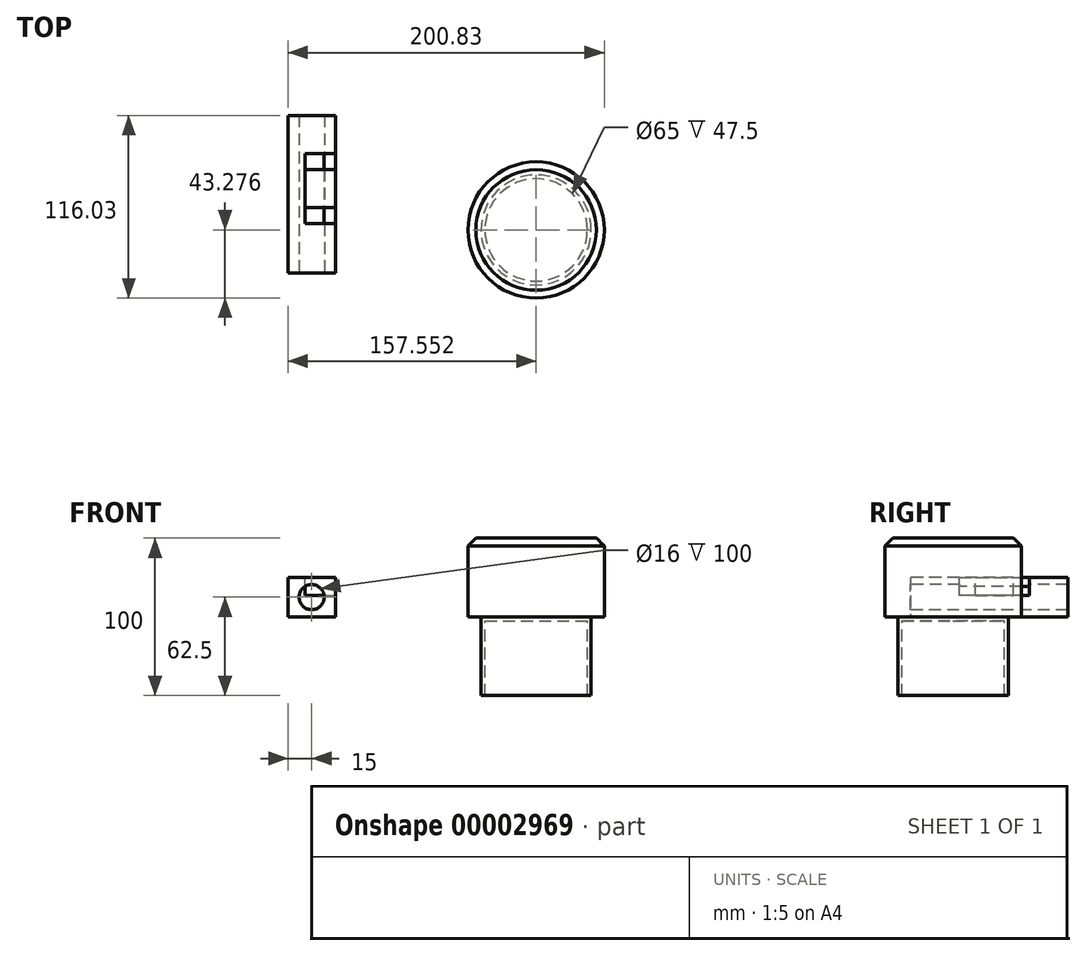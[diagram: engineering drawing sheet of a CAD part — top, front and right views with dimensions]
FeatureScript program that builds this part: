
annotation { "Feature Type Name" : "Feature", "Feature Type Description" : "" }
export const myFeature = defineFeature(function(context is Context, id is Id, definition is map)
    precondition{}
    {
        {
            var Q0;
            Q0=qCreatedBy(makeId("Top.planeOp"),FACE);
            var sketch = newSketch(context, id + "F0", { "sketchPlane" : qUnion([Q0])});
            skLineSegment(sketch, "E0.bottom", {"start": v(0, 0) * mm, "end": v(30, 0) * mm});
            skLineSegment(sketch, "E0.top", {"start": v(0, -100) * mm, "end": v(30, -100) * mm});
            skLineSegment(sketch, "E0.left", {"start": v(0, 0) * mm, "end": v(0, -100) * mm});
            skLineSegment(sketch, "E0.right", {"start": v(30, 0) * mm, "end": v(30, -100) * mm});
            skCircle(sketch, "E1", {"center": v(157.55, -72.75) * mm, "radius": 43.28 * mm});
            skSolve(sketch);
        }
        {
            var Q0;
            Q0=makeQuery(id+"F0.imprint","IMPRINT",FACE,{"disambiguationData":[TD([[makeQuery(id+"F0.imprint","IMPRINT",EDGE,{"derivedFrom":sQuery(id+"F0.wireOp",EDGE,"E0.bottom")}),-1.0]])]});
            var Q1;
            Q1=makeQuery(id+"F0.imprint","IMPRINT",FACE,{"disambiguationData":[TD([[makeQuery(id+"F0.imprint","IMPRINT",EDGE,{"derivedFrom":sQuery(id+"F0.wireOp",EDGE,"E1")}),1.0]])]});
            extrude(context, id + "F1", {"entities" : qUnion([Q0, Q1]), "depth" : 25 * mm});
        }
        {
            var Q0;
            Q0=makeQuery(id+"F1.opExtrude","SWEPT_FACE",FACE,{"disambiguationData":[OSD([sQuery(id+"F0.wireOp",EDGE,"E0.top")])]});
            var sketch = newSketch(context, id + "F2", { "sketchPlane" : qUnion([Q0])});
            skCircle(sketch, "E2", {"center": v(15, 12.5) * mm, "radius": 8 * mm});
            skLineSegment(sketch, "E3", {"start": v(30, 25) * mm, "end": v(0, 0) * mm});
            skSolve(sketch);
        }
        {
            var Q0;
            {var subQ0=sQuery(id+"F2.wireOp",EDGE,"E3");var subQ1=sQuery(id+"F2.wireOp",EDGE,"E2");var subQ3=makeQuery(id+"F2.imprint","INTERSECT",VERTEX,{"disambiguationData":[OD(0.0)],"derivedFrom":[subQ1,subQ0]});Q0=qUnion([makeQuery(id+"F2.imprint","IMPRINT",FACE,{"disambiguationData":[TD([[makeQuery(id+"F2.imprint","IMPRINT",EDGE,{"disambiguationData":[TD([[subQ3,-1.0]])],"derivedFrom":subQ1}),1.0]])]}),makeQuery(id+"F2.imprint","IMPRINT",FACE,{"disambiguationData":[TD([[makeQuery(id+"F2.imprint","IMPRINT",EDGE,{"disambiguationData":[TD([[subQ3,1.0]])],"derivedFrom":subQ1}),1.0]])]})]);}
            extrude(context, id + "F3", {"entities" : qUnion([Q0]), "operationType" : NewBodyOperationType.REMOVE, "endBound" : BoundingType.THROUGH_ALL, "oppositeDirection" : true, "depth" : 25 * mm});
        }
        {
            var Q0;
            Q0=makeQuery(id+"F1.opExtrude","CAP_FACE",FACE,{"disambiguationData":[OSD([sQuery(id+"F0.wireOp",EDGE,"E1")])],"isStart":true});
            var sketch = newSketch(context, id + "F4", { "sketchPlane" : qUnion([Q0])});
            skCircle(sketch, "E4", {"center": v(157.55, 72.75) * mm, "radius": 35 * mm});
            skSolve(sketch);
        }
        {
            var Q0;
            Q0=makeQuery(id+"F4.imprint","IMPRINT",FACE,{"disambiguationData":[TD([[makeQuery(id+"F4.imprint","IMPRINT",EDGE,{"derivedFrom":sQuery(id+"F4.wireOp",EDGE,"E4")}),1.0]])]});
            extrude(context, id + "F5", {"entities" : qUnion([Q0]), "depth" : 50 * mm});
        }
        {
            var Q0;
            Q0=makeQuery(id+"F1.opExtrude","CAP_FACE",FACE,{"disambiguationData":[OSD([sQuery(id+"F0.wireOp",EDGE,"E1")])],"isStart":false});
            extrude(context, id + "F6", {"entities" : qUnion([Q0]), "operationType" : NewBodyOperationType.ADD, "depth" : 25 * mm});
        }
        {
            var Q0;
            Q0=makeQuery(id+"F6.opExtrude","CAP_FACE",FACE,{"disambiguationData":[OSD([sQuery(id+"F0.wireOp",EDGE,"E1")])],"isStart":false});
            chamfer(context, id + "F7", {"entities" : qUnion([Q0]), "width" : 5 * mm, "tangentPropagation" : true});
        }
        {
            var Q0;
            Q0=makeQuery(id+"F5.opExtrude","CAP_FACE",FACE,{"disambiguationData":[OSD([sQuery(id+"F4.wireOp",EDGE,"E4")])],"isStart":false});
            shell(context, id + "F8", {"entities" : qUnion([Q0]), "thickness" : 2.5 * mm});
        }
        {
            var Q0;
            Q0=makeQuery(id+"F1.opExtrude","CAP_FACE",FACE,{"disambiguationData":[OSD([sQuery(id+"F0.wireOp",EDGE,"E0.bottom"),sQuery(id+"F0.wireOp",EDGE,"E0.top"),sQuery(id+"F0.wireOp",EDGE,"E0.left"),sQuery(id+"F0.wireOp",EDGE,"E0.right")])],"isStart":false});
            var sketch = newSketch(context, id + "F9", { "sketchPlane" : qUnion([Q0])});
            skLineSegment(sketch, "E5.bottom", {"start": v(10.71, -58.64) * mm, "end": v(30, -58.64) * mm});
            skLineSegment(sketch, "E5.top", {"start": v(10.71, -34.43) * mm, "end": v(30, -34.43) * mm});
            skLineSegment(sketch, "E5.left", {"start": v(10.71, -58.64) * mm, "end": v(10.71, -34.43) * mm});
            skLineSegment(sketch, "E5.right", {"start": v(30, -58.64) * mm, "end": v(30, -34.43) * mm});
            skSolve(sketch);
        }
        {
            var Q0;
            Q0=makeQuery(id+"F9.imprint","IMPRINT",FACE,{"disambiguationData":[TD([[makeQuery(id+"F9.imprint","IMPRINT",EDGE,{"derivedFrom":sQuery(id+"F9.wireOp",EDGE,"E5.bottom")}),1.0]])]});
            extrude(context, id + "F10", {"entities" : qUnion([Q0]), "oppositeDirection" : true, "depth" : 11.33 * mm});
        }
        {
            var Q0;
            Q0=makeQuery(id+"F10.opExtrude","SWEPT_BODY",BODY,{"disambiguationData":[OSD([sQuery(id+"F9.wireOp",EDGE,"E5.bottom"),sQuery(id+"F9.wireOp",EDGE,"E5.top"),sQuery(id+"F9.wireOp",EDGE,"E5.left"),sQuery(id+"F9.wireOp",EDGE,"E5.right")])]});
            var Q1;
            Q1=makeQuery(id+"F1.opExtrude","SWEPT_BODY",BODY,{"disambiguationData":[OSD([sQuery(id+"F0.wireOp",EDGE,"E0.bottom"),sQuery(id+"F0.wireOp",EDGE,"E0.top"),sQuery(id+"F0.wireOp",EDGE,"E0.left"),sQuery(id+"F0.wireOp",EDGE,"E0.right")])]});
            var Q2;
            Q2=makeQuery(id+"F10.opExtrude","SWEPT_FACE",FACE,{"disambiguationData":[OSD([sQuery(id+"F9.wireOp",EDGE,"E5.bottom")])]});
            var Q3;
            Q3=makeQuery(id+"F10.opExtrude","SWEPT_FACE",FACE,{"disambiguationData":[OSD([sQuery(id+"F9.wireOp",EDGE,"E5.top")])]});
            booleanBodies(context, id + "F11", {"operationType" : BooleanOperationType.SUBTRACTION, "tools" : qUnion([Q0]), "targets" : qUnion([Q1]), "offset" : true, "entitiesToOffset" : qUnion([Q2, Q3]), "offsetDistance" : 10 * mm, "keepTools" : true, "reFillet" : true});
        }
    });
